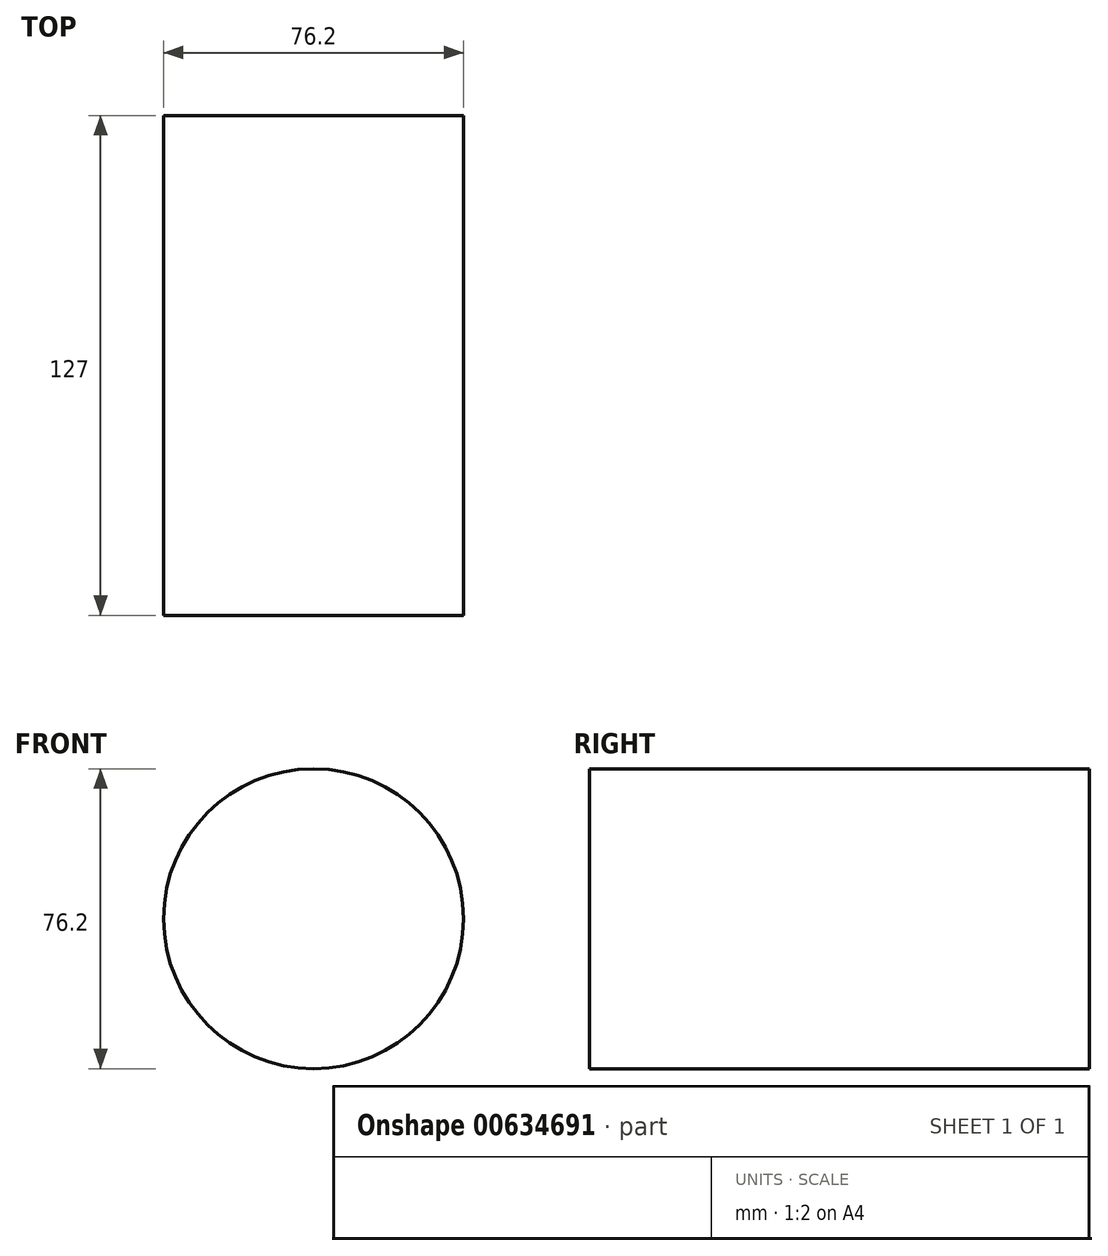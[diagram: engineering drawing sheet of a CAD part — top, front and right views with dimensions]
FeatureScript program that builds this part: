
annotation { "Feature Type Name" : "Feature", "Feature Type Description" : "" }
export const myFeature = defineFeature(function(context is Context, id is Id, definition is map)
    precondition{}
    {
        {
            var Q0;
            Q0=qCreatedBy(makeId("Front.planeOp"),FACE);
            var sketch = newSketch(context, id + "F0", { "sketchPlane" : qUnion([Q0])});
            skCircle(sketch, "E0", {"center": v(0, 0) * mm, "radius": 38.1 * mm});
            skSolve(sketch);
        }
        {
            var Q0;
            Q0=makeQuery(id+"F0.imprint","IMPRINT",FACE,{"disambiguationData":[TD([[makeQuery(id+"F0.imprint","IMPRINT",EDGE,{"derivedFrom":sQuery(id+"F0.wireOp",EDGE,"E0")}),1.0]])]});
            extrude(context, id + "F1", {"entities" : qUnion([Q0]), "depth" : 127 * mm, "offsetDistance" : 25.4 * mm});
        }
    });
